# Revit family: EBRME6-R2X115-30xx-SM
name_source: partatom
category: Leuchten
revit_build: Autodesk Revit 2017 (Build: 20190508_0315(x64)
units: mm (PartAtom-declared; Revit-internal decimal feet)

## family parameters
Basisbauteil = Fläche
Beim Laden mit Abzugskörper schneiden = Nein
Bemaßung runder Anschluss = Durchmesser verwenden
Gemeinsam genutzt = Nein
Lichtquelle = Ja
OmniClass-Nummer = 23.80.70.11
OmniClass-Titel = Luminaries for Internal Lighting
Raumberechnungspunkt = Nein
Teiletyp = Normal

## types (2) — shared parameters
Baugruppenkennzeichen = D5020200
Datei für fotometrisches Netz = EBRME6-R2x14535ND-SM.IES
Emissionsform beim Rendern sichtbar = Nein
Farbfilter = 16777215
Farbtemperaturverschiebung bei Dämpfen der Lampe = <Keine Auswahl>
Hersteller = RIDI Leuchten GmbH
Lampe = LED
Neigungswinkel = 90.00°
Scheinlast = 70 VA
URL = www.ridi.de
Von Breite des Rechtecks ausssenden = 1162 mm  [stored 3.81234 ft]
Von Länge des Rechtecks aussenden = 258 mm  [stored 0.846457 ft]
brand = RIDI
conformity mark = CE
electrical safety class = 1
height = 60 mm  [stored 0.19685 ft]
ingress protection (IP) code = IP20
length = 1197 mm
nominal frequency = 50-60Hz
nominal voltage = 230
rated input power = 70
voltage type (AC, DC, UC) = AC
weight = 4,42 kg
width = 297 mm  [stored 0.974409 ft]
zero-valued in all types: Vorgabe-Ansicht

## per-type parameters (varying)
| type | Modell |
| EBRME6-R2X115/30ND-SM | 0850054 |
| EBRME6-R2X115/30DA-SM | 0860054 |

note: column(s) folded — value = type name in every type: product name

note: [stored X ft] marks values corroborated as IEEE doubles in the binary element streams (Revit-internal decimal feet)
